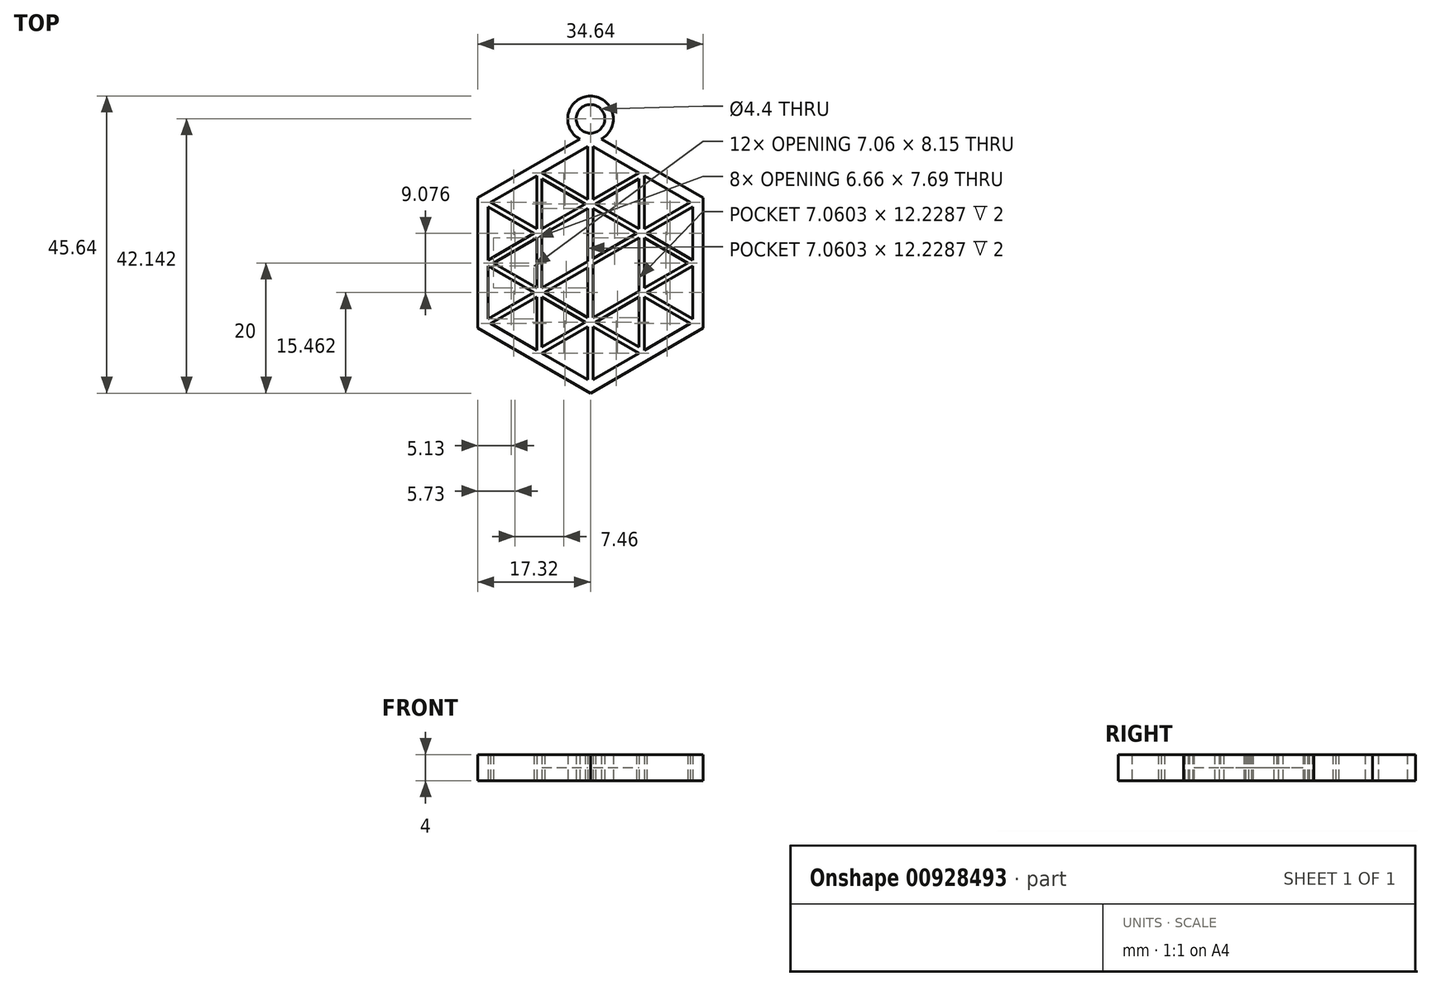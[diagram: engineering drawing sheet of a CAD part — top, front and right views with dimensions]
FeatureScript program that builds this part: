
annotation { "Feature Type Name" : "Feature", "Feature Type Description" : "" }
export const myFeature = defineFeature(function(context is Context, id is Id, definition is map)
    precondition{}
    {
        {
            var Q0;
            Q0=qCreatedBy(makeId("Top.planeOp"),FACE);
            var sketch = newSketch(context, id + "F0", { "sketchPlane" : qUnion([Q0])});
            skLineSegment(sketch, "E0.0", {"start": v(1.64, 19.05) * mm, "end": v(17.32, 10) * mm});
            skLineSegment(sketch, "E0.1", {"start": v(17.32, 10) * mm, "end": v(17.32, -10) * mm});
            skLineSegment(sketch, "E0.2", {"start": v(17.32, -10) * mm, "end": v(0, -20) * mm});
            skLineSegment(sketch, "E0.3", {"start": v(0, -20) * mm, "end": v(-17.32, -10) * mm});
            skLineSegment(sketch, "E0.4", {"start": v(-17.32, -10) * mm, "end": v(-17.32, 10) * mm});
            skLineSegment(sketch, "E0.5", {"start": v(-17.32, 10) * mm, "end": v(-1.64, 19.05) * mm});
            skLineSegment(sketch, "E1.0", {"start": v(0.4, 17.92) * mm, "end": v(7.46, 13.85) * mm});
            skLineSegment(sketch, "E1.1", {"start": v(15.72, 8.61) * mm, "end": v(15.72, 0.46) * mm});
            skLineSegment(sketch, "E1.2", {"start": v(15.32, -9.3) * mm, "end": v(8.26, -13.38) * mm});
            skLineSegment(sketch, "E1.3", {"start": v(-0.4, -17.92) * mm, "end": v(-7.46, -13.85) * mm});
            skLineSegment(sketch, "E1.4", {"start": v(-15.72, -8.61) * mm, "end": v(-15.72, -0.46) * mm});
            skLineSegment(sketch, "E1.5", {"start": v(-15.32, 9.3) * mm, "end": v(-8.26, 13.38) * mm});
            skLineSegment(sketch, "E2.0", {"start": v(8.26, -13.38) * mm, "end": v(8.26, -5.23) * mm});
            skLineSegment(sketch, "E3.0", {"start": v(7.46, -12.92) * mm, "end": v(7.46, -5.23) * mm});
            skLineSegment(sketch, "E4.0", {"start": v(0.4, -17.92) * mm, "end": v(0.4, -9.77) * mm});
            skLineSegment(sketch, "E5.0", {"start": v(-0.4, -17.92) * mm, "end": v(-0.4, -9.77) * mm});
            skLineSegment(sketch, "E6.0", {"start": v(-7.46, -12.92) * mm, "end": v(-7.46, -5.23) * mm});
            skLineSegment(sketch, "E7.0", {"start": v(-8.26, -13.38) * mm, "end": v(-8.26, -5.23) * mm});
            skLineSegment(sketch, "E8.0", {"start": v(-7.46, -13.85) * mm, "end": v(-0.4, -9.77) * mm});
            skLineSegment(sketch, "E9.0", {"start": v(-15.32, -9.3) * mm, "end": v(-8.26, -5.23) * mm});
            skLineSegment(sketch, "E10.0", {"start": v(-14.92, 0) * mm, "end": v(-8.26, 3.85) * mm});
            skLineSegment(sketch, "E11.0", {"start": v(-15.72, 0.46) * mm, "end": v(-8.66, 4.54) * mm});
            skLineSegment(sketch, "E12.0", {"start": v(-15.72, -8.61) * mm, "end": v(-8.66, -4.54) * mm});
            skLineSegment(sketch, "E13.0", {"start": v(-7.46, -12.92) * mm, "end": v(-0.8, -9.08) * mm});
            skLineSegment(sketch, "E14.0", {"start": v(15.72, -8.61) * mm, "end": v(8.66, -4.54) * mm});
            skLineSegment(sketch, "E15.0", {"start": v(7.46, -12.92) * mm, "end": v(0.8, -9.08) * mm});
            skLineSegment(sketch, "E16.0", {"start": v(14.92, 0) * mm, "end": v(8.26, 3.85) * mm});
            skLineSegment(sketch, "E17.0", {"start": v(15.32, -9.3) * mm, "end": v(8.26, -5.23) * mm});
            skLineSegment(sketch, "E18.0", {"start": v(7.46, -13.85) * mm, "end": v(0.4, -9.77) * mm});
            skLineSegment(sketch, "E19.trimOffspring", {"start": v(15.72, 0.46) * mm, "end": v(8.66, 4.54) * mm});
            skLineSegment(sketch, "E20.trimOffspring", {"start": v(15.72, -0.46) * mm, "end": v(15.72, -8.61) * mm});
            skLineSegment(sketch, "E21.trimOffspring", {"start": v(7.46, -13.85) * mm, "end": v(0.4, -17.92) * mm});
            skLineSegment(sketch, "E22.trimOffspring", {"start": v(-8.26, -13.38) * mm, "end": v(-15.32, -9.3) * mm});
            skLineSegment(sketch, "E23.trimOffspring", {"start": v(-15.72, 0.46) * mm, "end": v(-15.72, 8.61) * mm});
            skLineSegment(sketch, "E24.trimOffspring", {"start": v(-7.46, 13.85) * mm, "end": v(-0.4, 17.92) * mm});
            skLineSegment(sketch, "E25.trimOffspring", {"start": v(8.26, 13.38) * mm, "end": v(15.32, 9.3) * mm});
            skLineSegment(sketch, "E26.trimOffspring", {"start": v(-8.66, 4.54) * mm, "end": v(-15.72, 8.61) * mm});
            skLineSegment(sketch, "E27.trimOffspring", {"start": v(-0.4, 9.77) * mm, "end": v(-7.46, 13.85) * mm});
            skLineSegment(sketch, "E28.trimOffspring", {"start": v(0.4, 9.77) * mm, "end": v(7.46, 13.85) * mm});
            skLineSegment(sketch, "E29.trimOffspring", {"start": v(-0.4, 9.77) * mm, "end": v(-0.4, 17.92) * mm});
            skLineSegment(sketch, "E30.trimOffspring", {"start": v(-0.8, 9.08) * mm, "end": v(-7.46, 12.92) * mm});
            skLineSegment(sketch, "E31.trimOffspring", {"start": v(0.8, 9.08) * mm, "end": v(7.46, 12.92) * mm});
            skLineSegment(sketch, "E32.trimOffspring", {"start": v(0.4, 9.77) * mm, "end": v(0.4, 17.92) * mm});
            skLineSegment(sketch, "E33.trimOffspring", {"start": v(7.46, 5.23) * mm, "end": v(0.8, 9.08) * mm});
            skLineSegment(sketch, "E34.trimOffspring", {"start": v(8.26, 5.23) * mm, "end": v(15.32, 9.3) * mm});
            skLineSegment(sketch, "E35.trimOffspring", {"start": v(7.46, 5.23) * mm, "end": v(7.46, 12.92) * mm});
            skLineSegment(sketch, "E36.trimOffspring", {"start": v(8.26, 5.23) * mm, "end": v(8.26, 13.38) * mm});
            skLineSegment(sketch, "E37.trimOffspring", {"start": v(8.66, 4.54) * mm, "end": v(15.72, 8.61) * mm});
            skLineSegment(sketch, "E38.trimOffspring", {"start": v(7.06, 4.54) * mm, "end": v(0.4, 8.38) * mm});
            skLineSegment(sketch, "E39.trimOffspring", {"start": v(-7.46, 5.23) * mm, "end": v(-7.46, 12.92) * mm});
            skLineSegment(sketch, "E40.trimOffspring", {"start": v(-7.46, 4.3) * mm, "end": v(-0.4, 8.38) * mm});
            skLineSegment(sketch, "E41.trimOffspring", {"start": v(-8.26, 5.23) * mm, "end": v(-8.26, 13.38) * mm});
            skLineSegment(sketch, "E42.trimOffspring", {"start": v(-7.46, 5.23) * mm, "end": v(-0.8, 9.08) * mm});
            skLineSegment(sketch, "E43.trimOffspring", {"start": v(-8.26, 5.23) * mm, "end": v(-15.32, 9.3) * mm});
            skLineSegment(sketch, "E44.trimOffspring", {"start": v(-0.4, 0.23) * mm, "end": v(-0.4, 8.38) * mm});
            skLineSegment(sketch, "E45.trimOffspring", {"start": v(0.4, -0.23) * mm, "end": v(7.46, 3.85) * mm});
            skLineSegment(sketch, "E46.trimOffspring", {"start": v(0.4, 0.7) * mm, "end": v(0.4, 8.38) * mm});
            skLineSegment(sketch, "E47.trimOffspring", {"start": v(0.4, 0.7) * mm, "end": v(7.06, 4.54) * mm});
            skLineSegment(sketch, "E48.trimOffspring", {"start": v(7.46, -4.3) * mm, "end": v(7.46, 3.85) * mm});
            skLineSegment(sketch, "E49.trimOffspring", {"start": v(8.26, -3.85) * mm, "end": v(8.26, 3.85) * mm});
            skLineSegment(sketch, "E50.trimOffspring", {"start": v(8.66, -4.54) * mm, "end": v(15.72, -0.46) * mm});
            skLineSegment(sketch, "E51.trimOffspring", {"start": v(8.26, -3.85) * mm, "end": v(14.92, 0) * mm});
            skLineSegment(sketch, "E52.trimOffspring", {"start": v(-8.26, -3.85) * mm, "end": v(-14.92, 0) * mm});
            skLineSegment(sketch, "E53.trimOffspring", {"start": v(-7.46, -3.85) * mm, "end": v(-0.4, 0.23) * mm});
            skLineSegment(sketch, "E54.trimOffspring", {"start": v(-8.66, -4.54) * mm, "end": v(-15.72, -0.46) * mm});
            skLineSegment(sketch, "E55.trimOffspring", {"start": v(-7.06, -4.54) * mm, "end": v(-0.4, -0.7) * mm});
            skLineSegment(sketch, "E56.trimOffspring", {"start": v(-7.46, -3.85) * mm, "end": v(-7.46, 4.3) * mm});
            skLineSegment(sketch, "E57.trimOffspring", {"start": v(-8.26, -3.85) * mm, "end": v(-8.26, 3.85) * mm});
            skLineSegment(sketch, "E58.trimOffspring", {"start": v(0.4, -8.38) * mm, "end": v(7.46, -4.3) * mm});
            skLineSegment(sketch, "E59.trimOffspring", {"start": v(0.8, -9.08) * mm, "end": v(7.46, -5.23) * mm});
            skLineSegment(sketch, "E60.trimOffspring", {"start": v(-0.8, -9.08) * mm, "end": v(-7.46, -5.23) * mm});
            skLineSegment(sketch, "E61.trimOffspring", {"start": v(-0.4, -8.38) * mm, "end": v(-0.4, -0.7) * mm});
            skLineSegment(sketch, "E62.trimOffspring", {"start": v(0.4, -8.38) * mm, "end": v(0.4, -0.23) * mm});
            skLineSegment(sketch, "E63.trimOffspring", {"start": v(-0.4, -8.38) * mm, "end": v(-7.06, -4.54) * mm});
            skArc(sketch, "E64", {"start": v(1.64, 19.05) * mm, "mid": v(0, 25.64) * mm, "end": v(-1.64, 19.05) * mm});
            skCircle(sketch, "E65", {"center": v(0, 22.14) * mm, "radius": 2.2 * mm});
            skPoint(sketch, "E66.orphan", {"position": v(0, 20) * mm});
            skSolve(sketch);
        }
        {
            var Q0;
            Q0 = qSketchRegion(id + "F0", true);
            extrude(context, id + "F1", {"entities" : qUnion([Q0]), "depth" : 4 * mm, "offsetDistance" : 25 * mm});
        }
        {
            var Q0;
            Q0=makeQuery(id+"F1.opExtrude","CAP_FACE",FACE,{"disambiguationData":[OSD([sQuery(id+"F0.wireOp",EDGE,"E0.0"),sQuery(id+"F0.wireOp",EDGE,"E0.1"),sQuery(id+"F0.wireOp",EDGE,"E0.2"),sQuery(id+"F0.wireOp",EDGE,"E0.3"),sQuery(id+"F0.wireOp",EDGE,"E0.4"),sQuery(id+"F0.wireOp",EDGE,"E0.5"),sQuery(id+"F0.wireOp",EDGE,"E1.0"),sQuery(id+"F0.wireOp",EDGE,"E1.1"),sQuery(id+"F0.wireOp",EDGE,"E1.2"),sQuery(id+"F0.wireOp",EDGE,"E1.3"),sQuery(id+"F0.wireOp",EDGE,"E1.4"),sQuery(id+"F0.wireOp",EDGE,"E1.5"),sQuery(id+"F0.wireOp",EDGE,"E2.0"),sQuery(id+"F0.wireOp",EDGE,"E3.0"),sQuery(id+"F0.wireOp",EDGE,"E4.0"),sQuery(id+"F0.wireOp",EDGE,"E5.0"),sQuery(id+"F0.wireOp",EDGE,"E6.0"),sQuery(id+"F0.wireOp",EDGE,"E7.0"),sQuery(id+"F0.wireOp",EDGE,"E8.0"),sQuery(id+"F0.wireOp",EDGE,"E9.0"),sQuery(id+"F0.wireOp",EDGE,"E10.0"),sQuery(id+"F0.wireOp",EDGE,"E11.0"),sQuery(id+"F0.wireOp",EDGE,"E12.0"),sQuery(id+"F0.wireOp",EDGE,"E13.0"),sQuery(id+"F0.wireOp",EDGE,"E14.0"),sQuery(id+"F0.wireOp",EDGE,"E15.0"),sQuery(id+"F0.wireOp",EDGE,"E16.0"),sQuery(id+"F0.wireOp",EDGE,"E17.0"),sQuery(id+"F0.wireOp",EDGE,"E18.0"),sQuery(id+"F0.wireOp",EDGE,"E19.trimOffspring"),sQuery(id+"F0.wireOp",EDGE,"E20.trimOffspring"),sQuery(id+"F0.wireOp",EDGE,"E21.trimOffspring"),sQuery(id+"F0.wireOp",EDGE,"E22.trimOffspring"),sQuery(id+"F0.wireOp",EDGE,"E23.trimOffspring"),sQuery(id+"F0.wireOp",EDGE,"E24.trimOffspring"),sQuery(id+"F0.wireOp",EDGE,"E25.trimOffspring"),sQuery(id+"F0.wireOp",EDGE,"E26.trimOffspring"),sQuery(id+"F0.wireOp",EDGE,"E27.trimOffspring"),sQuery(id+"F0.wireOp",EDGE,"E28.trimOffspring"),sQuery(id+"F0.wireOp",EDGE,"E29.trimOffspring"),sQuery(id+"F0.wireOp",EDGE,"E30.trimOffspring"),sQuery(id+"F0.wireOp",EDGE,"E31.trimOffspring"),sQuery(id+"F0.wireOp",EDGE,"E32.trimOffspring"),sQuery(id+"F0.wireOp",EDGE,"E33.trimOffspring"),sQuery(id+"F0.wireOp",EDGE,"E34.trimOffspring"),sQuery(id+"F0.wireOp",EDGE,"E35.trimOffspring"),sQuery(id+"F0.wireOp",EDGE,"E36.trimOffspring"),sQuery(id+"F0.wireOp",EDGE,"E37.trimOffspring"),sQuery(id+"F0.wireOp",EDGE,"E38.trimOffspring"),sQuery(id+"F0.wireOp",EDGE,"E39.trimOffspring"),sQuery(id+"F0.wireOp",EDGE,"E40.trimOffspring"),sQuery(id+"F0.wireOp",EDGE,"E41.trimOffspring"),sQuery(id+"F0.wireOp",EDGE,"E42.trimOffspring"),sQuery(id+"F0.wireOp",EDGE,"E43.trimOffspring"),sQuery(id+"F0.wireOp",EDGE,"E44.trimOffspring"),sQuery(id+"F0.wireOp",EDGE,"E45.trimOffspring"),sQuery(id+"F0.wireOp",EDGE,"E46.trimOffspring"),sQuery(id+"F0.wireOp",EDGE,"E47.trimOffspring"),sQuery(id+"F0.wireOp",EDGE,"E48.trimOffspring"),sQuery(id+"F0.wireOp",EDGE,"E49.trimOffspring"),sQuery(id+"F0.wireOp",EDGE,"E50.trimOffspring"),sQuery(id+"F0.wireOp",EDGE,"E51.trimOffspring"),sQuery(id+"F0.wireOp",EDGE,"E52.trimOffspring"),sQuery(id+"F0.wireOp",EDGE,"E53.trimOffspring"),sQuery(id+"F0.wireOp",EDGE,"E54.trimOffspring"),sQuery(id+"F0.wireOp",EDGE,"E55.trimOffspring"),sQuery(id+"F0.wireOp",EDGE,"E56.trimOffspring"),sQuery(id+"F0.wireOp",EDGE,"E57.trimOffspring"),sQuery(id+"F0.wireOp",EDGE,"E58.trimOffspring"),sQuery(id+"F0.wireOp",EDGE,"E59.trimOffspring"),sQuery(id+"F0.wireOp",EDGE,"E60.trimOffspring"),sQuery(id+"F0.wireOp",EDGE,"E61.trimOffspring"),sQuery(id+"F0.wireOp",EDGE,"E62.trimOffspring"),sQuery(id+"F0.wireOp",EDGE,"E63.trimOffspring"),sQuery(id+"F0.wireOp",EDGE,"E64"),sQuery(id+"F0.wireOp",EDGE,"E65")])],"isStart":true});
            var sketch = newSketch(context, id + "F2", { "sketchPlane" : qUnion([Q0])});
            skLineSegment(sketch, "E67", {"start": v(7.46, -3.85) * mm, "end": v(7.46, 4.3) * mm});
            skLineSegment(sketch, "E68", {"start": v(7.46, 4.3) * mm, "end": v(0.4, 8.38) * mm});
            skLineSegment(sketch, "E69", {"start": v(0.4, 8.38) * mm, "end": v(0.4, 0.23) * mm});
            skLineSegment(sketch, "E70", {"start": v(0.4, 0.23) * mm, "end": v(7.46, -3.85) * mm});
            skLineSegment(sketch, "E71", {"start": v(-0.4, -8.38) * mm, "end": v(-0.4, -0.23) * mm});
            skLineSegment(sketch, "E72", {"start": v(-0.4, -0.23) * mm, "end": v(-7.46, 3.85) * mm});
            skLineSegment(sketch, "E73", {"start": v(-7.46, 3.85) * mm, "end": v(-7.46, -4.3) * mm});
            skLineSegment(sketch, "E74", {"start": v(-7.46, -4.3) * mm, "end": v(-0.4, -8.38) * mm});
            skSolve(sketch);
        }
        {
            var Q0;
            Q0 = qSketchRegion(id + "F2", true);
            extrude(context, id + "F3", {"entities" : qUnion([Q0]), "operationType" : NewBodyOperationType.ADD, "oppositeDirection" : true, "depth" : 2 * mm, "offsetDistance" : 25 * mm});
        }
    });
